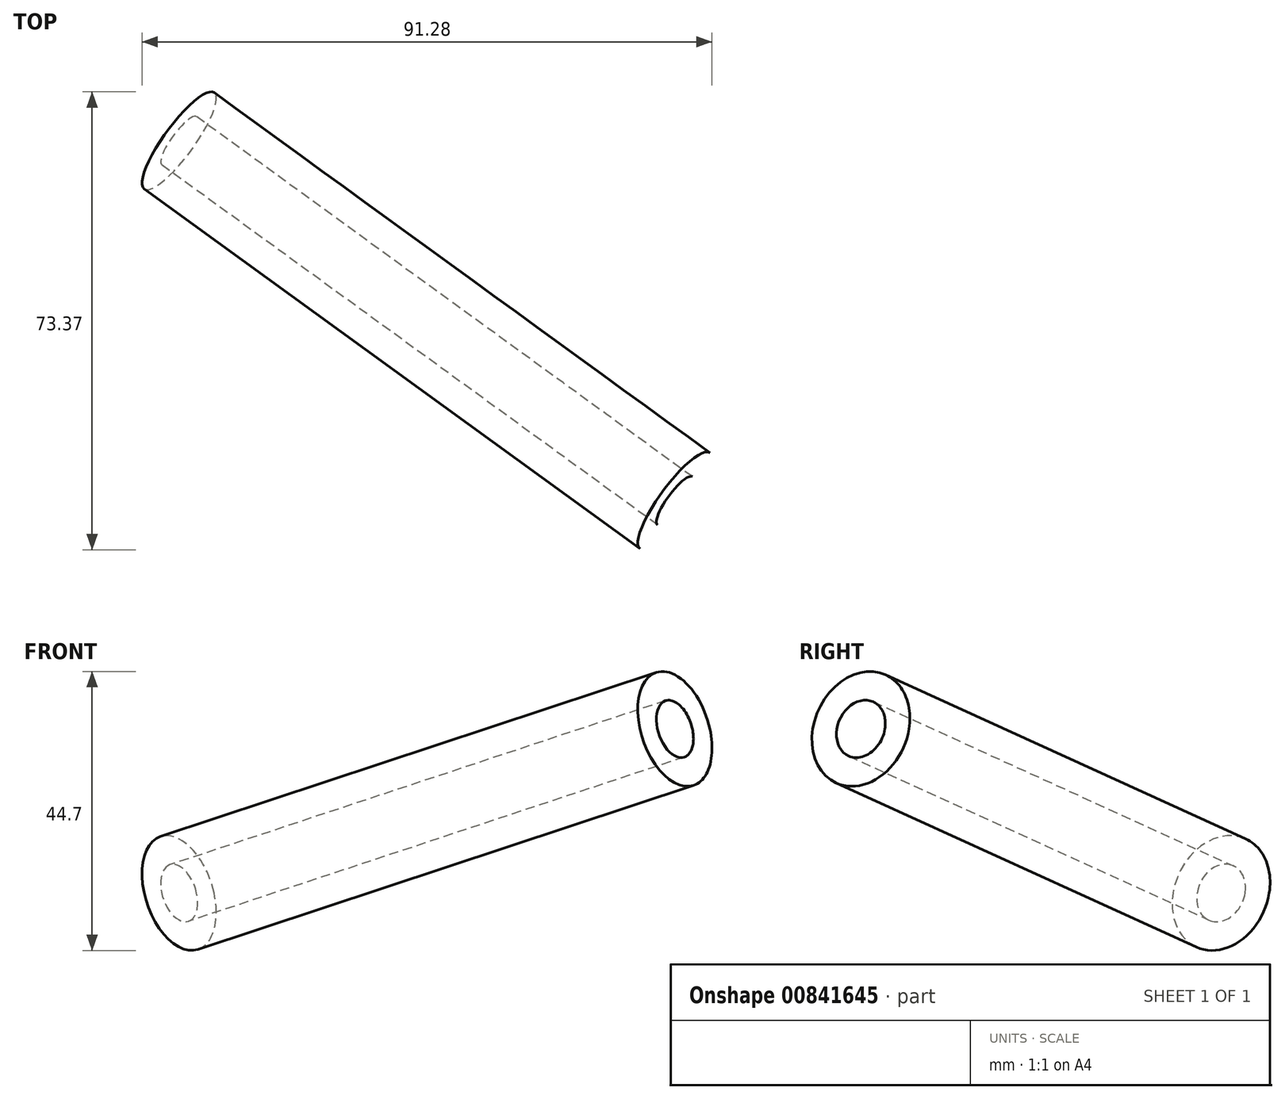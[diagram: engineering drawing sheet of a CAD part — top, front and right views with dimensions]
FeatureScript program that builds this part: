
annotation { "Feature Type Name" : "Feature", "Feature Type Description" : "" }
export const myFeature = defineFeature(function(context is Context, id is Id, definition is map)
    precondition{}
    {
        {
            var Q0;
            Q0=qCreatedBy(makeId("Top.planeOp"),FACE);
            var sketch = newSketch(context, id + "F0", { "sketchPlane" : qUnion([Q0])});
            skLineSegment(sketch, "E0", {"start": v(-101.9, 49.89) * mm, "end": v(-70.07, 93.7) * mm});
            skLineSegment(sketch, "E1", {"start": v(-92.38, -34.56) * mm, "end": v(-68.99, -65.31) * mm});
            skLineSegment(sketch, "E2", {"start": v(0, 0) * mm, "end": v(-144.53, 0) * mm, "construction": true});
            skLineSegment(sketch, "E3", {"start": v(0, -39.57) * mm, "end": v(0, 58.02) * mm, "construction": true});
            skSolve(sketch);
        }
        {
            var Q0;
            Q0=sQuery(id+"F0.wireOp",EDGE,"E0");
            cPlane(context, id + "F1", {"entities" : qUnion([Q0]), "cplaneType" : CPlaneType.LINE_ANGLE, "offset" : 25.4 * mm, "angle" : 75 * degree, "width" : 152.4 * mm, "height" : 152.4 * mm});
        }
        {
            var Q0;
            Q0=qCreatedBy(id+"F1.planeOp",FACE);
            var sketch = newSketch(context, id + "F2", { "sketchPlane" : qUnion([Q0])});
            skLineSegment(sketch, "E4", {"start": v(15.02, -7.33) * mm, "end": v(15.02, 86.65) * mm, "construction": true});
            skCircle(sketch, "E5", {"center": v(15.02, -7.33) * mm, "radius": 4.76 * mm});
            skCircle(sketch, "E6", {"center": v(15.02, -7.33) * mm, "radius": 9.53 * mm});
            skLineSegment(sketch, "E7", {"start": v(-76.01, 32.02) * mm, "end": v(47.99, 32.02) * mm, "construction": true});
            skSolve(sketch);
        }
        {
            var Q0;
            Q0=makeQuery(id+"F2.imprint","IMPRINT",FACE,{"disambiguationData":[TD([[makeQuery(id+"F2.imprint","IMPRINT",EDGE,{"derivedFrom":sQuery(id+"F2.wireOp",EDGE,"E5")}),-1.0]])]});
            extrude(context, id + "F3", {"entities" : qUnion([Q0]), "depth" : 101.6 * mm, "offsetDistance" : 25.4 * mm});
        }
    });
